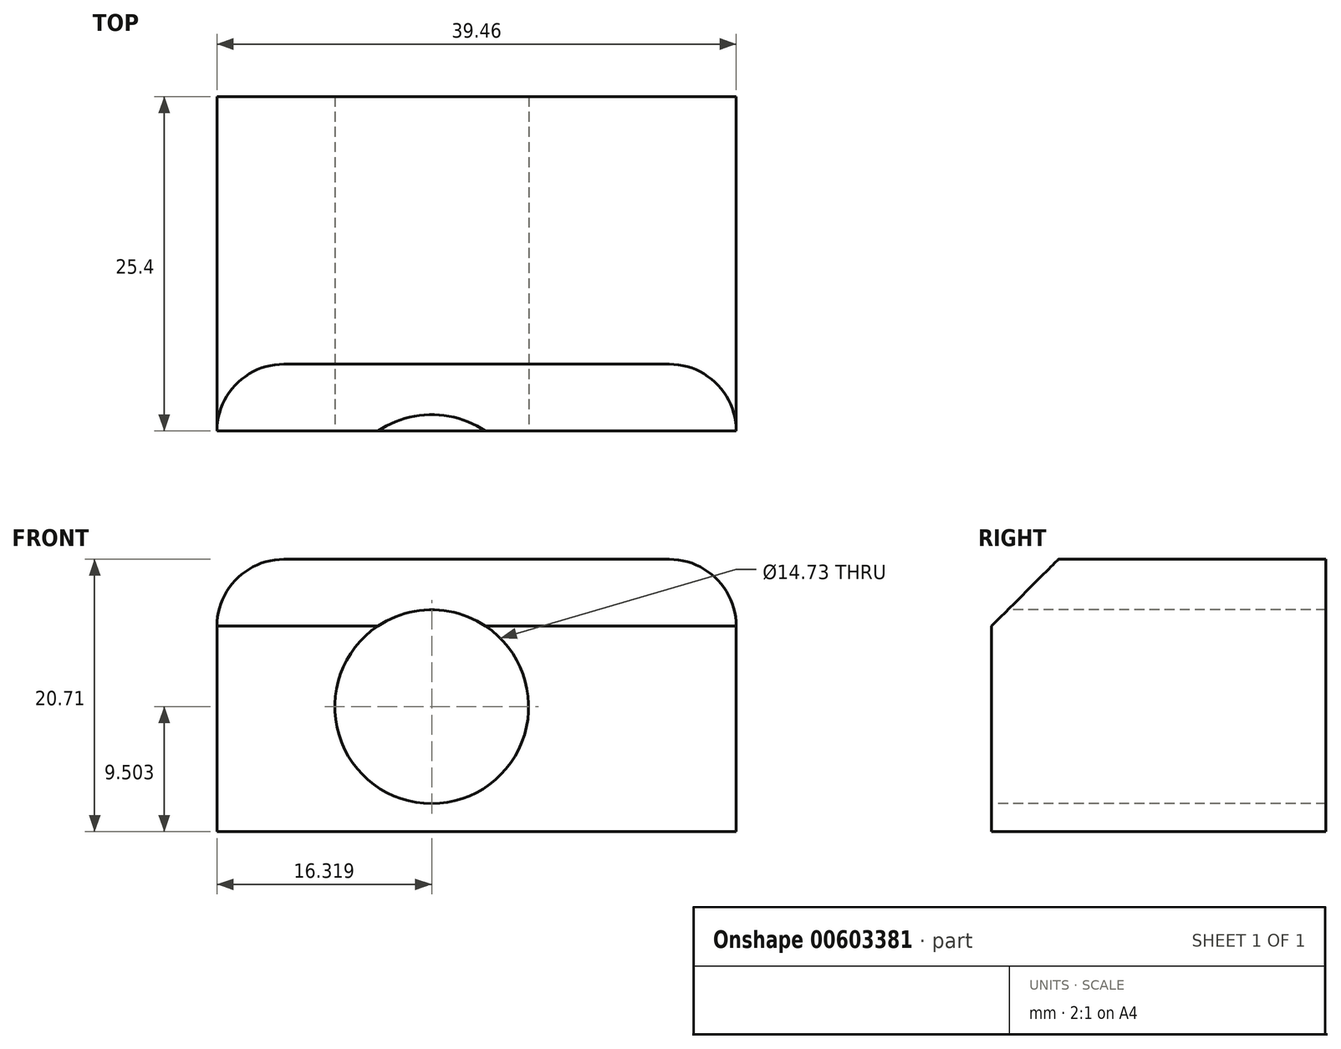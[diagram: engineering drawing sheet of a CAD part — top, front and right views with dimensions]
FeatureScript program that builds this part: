
annotation { "Feature Type Name" : "Feature", "Feature Type Description" : "" }
export const myFeature = defineFeature(function(context is Context, id is Id, definition is map)
    precondition{}
    {
        {
            var Q0;
            Q0=qCreatedBy(makeId("Front.planeOp"),FACE);
            var sketch = newSketch(context, id + "F0", { "sketchPlane" : qUnion([Q0])});
            skLineSegment(sketch, "E0.bottom", {"start": v(-26.67, 17.54) * mm, "end": v(12.79, 17.54) * mm});
            skLineSegment(sketch, "E0.top", {"start": v(-26.67, -3.17) * mm, "end": v(12.79, -3.17) * mm});
            skLineSegment(sketch, "E0.left", {"start": v(-26.67, 17.54) * mm, "end": v(-26.67, -3.17) * mm});
            skLineSegment(sketch, "E0.right", {"start": v(12.79, 17.54) * mm, "end": v(12.79, -3.17) * mm});
            skSolve(sketch);
        }
        {
            var Q0;
            Q0=makeQuery(id+"F0.imprint","IMPRINT",FACE,{"disambiguationData":[TD([[makeQuery(id+"F0.imprint","IMPRINT",EDGE,{"derivedFrom":sQuery(id+"F0.wireOp",EDGE,"E0.bottom")}),-1.0]])]});
            extrude(context, id + "F1", {"entities" : qUnion([Q0]), "depth" : 25.4 * mm, "offsetDistance" : 25.4 * mm});
        }
        {
            var Q0;
            Q0=makeQuery(id+"F1.opExtrude","CAP_FACE",FACE,{"disambiguationData":[OSD([sQuery(id+"F0.wireOp",EDGE,"E0.bottom"),sQuery(id+"F0.wireOp",EDGE,"E0.top"),sQuery(id+"F0.wireOp",EDGE,"E0.left"),sQuery(id+"F0.wireOp",EDGE,"E0.right")])],"isStart":false});
            var sketch = newSketch(context, id + "F2", { "sketchPlane" : qUnion([Q0])});
            skCircle(sketch, "E1", {"center": v(-10.35, 6.33) * mm, "radius": 7.36 * mm});
            skSolve(sketch);
        }
        {
            var Q0;
            Q0=makeQuery(id+"F2.imprint","IMPRINT",FACE,{"disambiguationData":[TD([[makeQuery(id+"F2.imprint","IMPRINT",EDGE,{"derivedFrom":sQuery(id+"F2.wireOp",EDGE,"E1")}),1.0]])]});
            var Q1;
            Q1=sQuery(id+"F2.wireOp",EDGE,"E1");
            extrude(context, id + "F3", {"entities" : qUnion([Q0]), "operationType" : NewBodyOperationType.REMOVE, "surfaceEntities" : qUnion([Q1]), "oppositeDirection" : true, "depth" : 25.4 * mm, "offsetDistance" : 25.4 * mm});
        }
        {
            var Q0;
            Q0=makeQuery(id+"F1.opExtrude","CAP_EDGE",EDGE,{"disambiguationData":[OSD([sQuery(id+"F0.wireOp",EDGE,"E0.bottom")])],"isStart":false});
            chamfer(context, id + "F4", {"entities" : qUnion([Q0]), "width" : 5.08 * mm, "tangentPropagation" : true});
        }
        {
            var Q0;
            Q0=makeQuery(id+"F1.opExtrude","SWEPT_EDGE",EDGE,{"disambiguationData":[OSD([sQuery(id+"F0.wireOp",EDGE,"E0.bottom"),sQuery(id+"F0.wireOp",EDGE,"E0.right")])]});
            fillet(context, id + "F5", {"entities" : qUnion([Q0]), "radius" : 5.08 * mm, "tangentPropagation" : true, "allowEdgeOverflow" : false});
        }
        {
            var Q0;
            Q0=makeQuery(id+"F1.opExtrude","SWEPT_EDGE",EDGE,{"disambiguationData":[OSD([sQuery(id+"F0.wireOp",EDGE,"E0.bottom"),sQuery(id+"F0.wireOp",EDGE,"E0.left")])]});
            fillet(context, id + "F6", {"entities" : qUnion([Q0]), "radius" : 5.08 * mm, "tangentPropagation" : true, "allowEdgeOverflow" : false});
        }
    });
